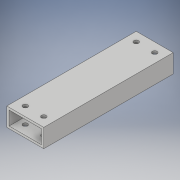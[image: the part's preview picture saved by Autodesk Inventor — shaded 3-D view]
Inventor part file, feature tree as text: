
AUTODESK INVENTOR PART (.ipt)
format: ipt  version: 2017 (Build 210142000, 142)  size: 119,296 bytes
history: native  units: in
note: dims shown in document units (in); Inventor stores cm internally (conversion verified against a paired STEP export)
features: sketch x2, extrude x1, hole x1
ambient origin geometry x8: Origin, YZ Plane, XZ Plane, XY Plane, X Axis, Y Axis, Z Axis, Center Point
bodies: Solid1 (feature_tree)
feature tree (4):
  extrude  "Extrusion1"  Depth=1.0in
  hole  "Hole1"  [1 undecoded]
  sketch  "Sketch1"  dims[d0=2.0in d1=1.0in]
  sketch  "Sketch2"  dims[d2=1.75in d3=0.75in d4=0.125in d5=0.125in d6=7.0in d7=0.0in d8=0.25in d9=0.5in d10=0.5in d11=0.25in d12=0.75in d13=0.375in d14=0.25in d15=0.5635in d16=1.0in d17=0.8108in]
note: 1 required parameter value undecoded (feature->parameter linkage not recoverable at this tier; creation-order binding heuristic only, values carry confidence <= 0.55)
